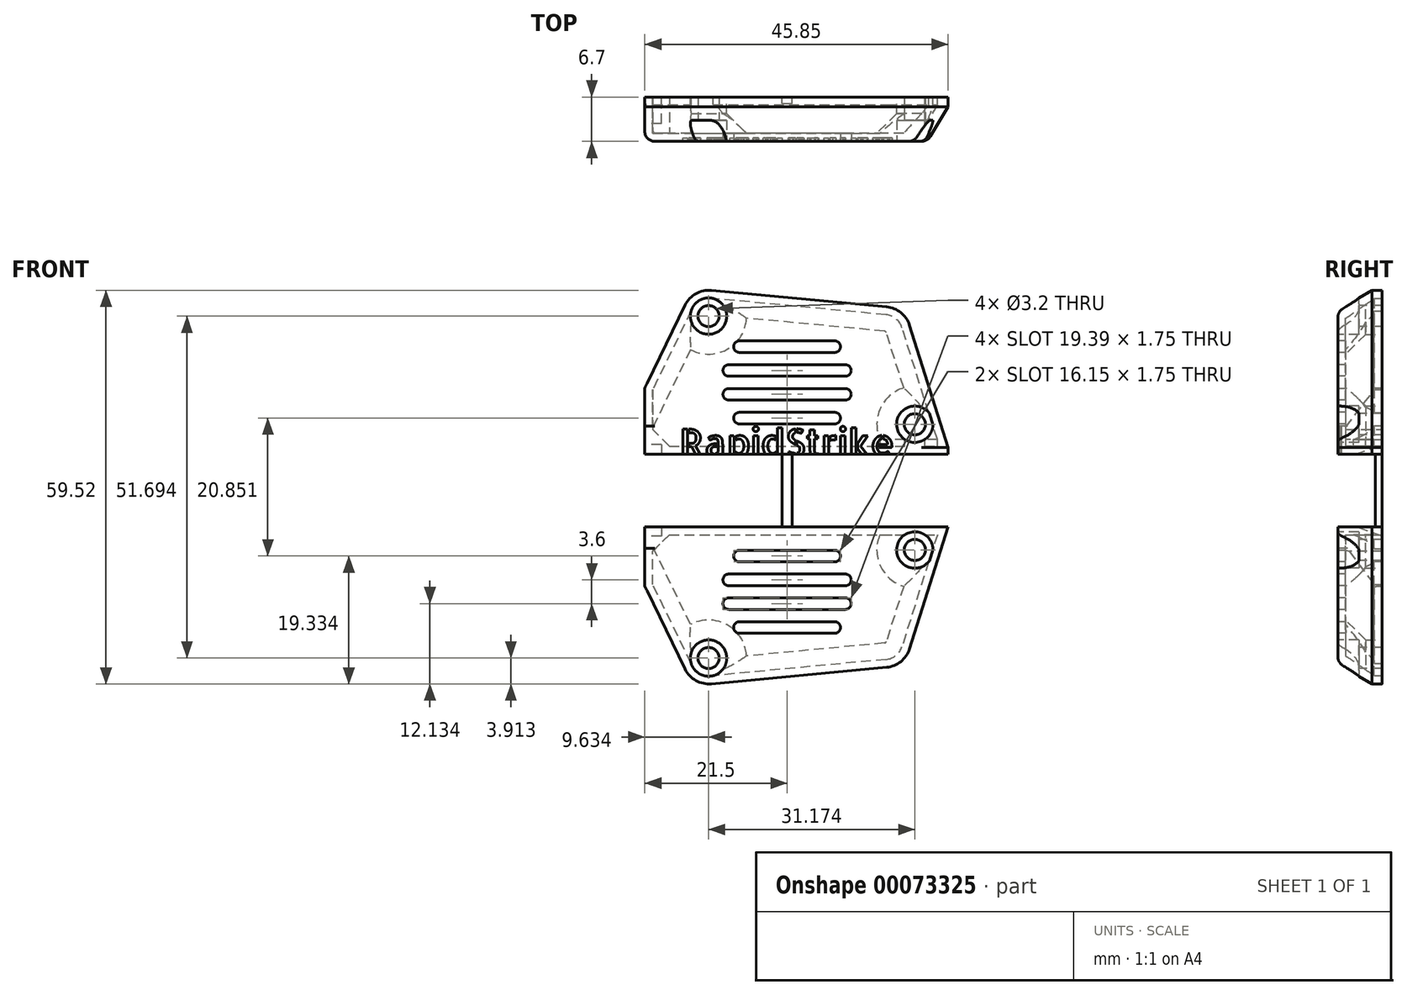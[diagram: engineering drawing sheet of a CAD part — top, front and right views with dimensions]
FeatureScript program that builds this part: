
annotation { "Feature Type Name" : "Feature", "Feature Type Description" : "" }
export const myFeature = defineFeature(function(context is Context, id is Id, definition is map)
    precondition{}
    {
        {
            var Q0;
            Q0=qCreatedBy(makeId("Front.planeOp"),FACE);
            var sketch = newSketch(context, id + "F0", { "sketchPlane" : qUnion([Q0])});
            skLineSegment(sketch, "E0", {"start": v(-21.5, 0) * mm, "end": v(21.5, 0) * mm, "construction": true});
            skLineSegment(sketch, "E1", {"start": v(24.35, -9) * mm, "end": v(17.7, 12) * mm});
            skLineSegment(sketch, "E2", {"start": v(17.7, 12) * mm, "end": v(-14.2, 15) * mm});
            skLineSegment(sketch, "E3", {"start": v(-14.2, 15) * mm, "end": v(-21.5, 0) * mm});
            skLineSegment(sketch, "E4", {"start": v(-21.5, 0) * mm, "end": v(-21.5, -9) * mm});
            skLineSegment(sketch, "E5", {"start": v(-21.5, -9) * mm, "end": v(24.35, -9) * mm});
            skSolve(sketch);
        }
        {
            var Q0;
            Q0=qCreatedBy(makeId("Front.planeOp"),FACE);
            var sketch = newSketch(context, id + "F1", { "sketchPlane" : qUnion([Q0])});
            skLineSegment(sketch, "E6.0", {"start": v(-21.5, 0) * mm, "end": v(21.5, 0) * mm});
            skLineSegment(sketch, "E6.1", {"start": v(24.35, -9) * mm, "end": v(18.5, 9.47) * mm});
            skLineSegment(sketch, "E6.2", {"start": v(15.06, 12.25) * mm, "end": v(-11.44, 14.74) * mm});
            skLineSegment(sketch, "E6.3", {"start": v(-15.41, 12.5) * mm, "end": v(-21.5, 0) * mm});
            skLineSegment(sketch, "E6.4", {"start": v(-21.5, 0) * mm, "end": v(-21.5, -9) * mm});
            skLineSegment(sketch, "E6.5", {"start": v(-21.5, -9) * mm, "end": v(24.35, -9) * mm});
            skPoint(sketch, "E7.visualSharp", {"position": v(-14.2, 15) * mm});
            skArc(sketch, "E7.filletArc", {"start": v(-11.44, 14.74) * mm, "mid": v(-13.78, 14.25) * mm, "end": v(-15.41, 12.5) * mm});
            skPoint(sketch, "E8.visualSharp", {"position": v(17.7, 12) * mm});
            skArc(sketch, "E8.filletArc", {"start": v(18.5, 9.47) * mm, "mid": v(17.2, 11.38) * mm, "end": v(15.06, 12.25) * mm});
            skSolve(sketch);
        }
        {
            var Q0;
            Q0 = qSketchRegion(id + "F1", true);
            extrude(context, id + "F2", {"entities" : qUnion([Q0]), "depth" : 6.7 * mm});
        }
        {
            var Q0;
            Q0=makeQuery(id+"F2.opExtrude","CAP_EDGE",EDGE,{"disambiguationData":[OSD([sQuery(id+"F1.wireOp",EDGE,"E6.3")])],"isStart":false});
            chamfer(context, id + "F3", {"entities" : qUnion([Q0]), "chamferType" : ChamferType.OFFSET_ANGLE, "width" : 3 * mm, "oppositeDirection" : false, "angle" : 60 * degree, "tangentPropagation" : true});
        }
        {
            var Q0;
            Q0=makeQuery(id+"F2.opExtrude","CAP_FACE",FACE,{"disambiguationData":[OSD([sQuery(id+"F1.wireOp",EDGE,"E6.1"),sQuery(id+"F1.wireOp",EDGE,"E6.2"),sQuery(id+"F1.wireOp",EDGE,"E6.3"),sQuery(id+"F1.wireOp",EDGE,"E6.4"),sQuery(id+"F1.wireOp",EDGE,"E6.5"),sQuery(id+"F1.wireOp",EDGE,"E7.filletArc"),sQuery(id+"F1.wireOp",EDGE,"E8.filletArc")])],"isStart":true});
            shell(context, id + "F4", {"entities" : qUnion([Q0]), "thickness" : 1.2 * mm});
        }
        {
            var Q0;
            Q0=makeQuery(id+"F2.opExtrude","CAP_FACE",FACE,{"disambiguationData":[OSD([sQuery(id+"F1.wireOp",EDGE,"E6.1"),sQuery(id+"F1.wireOp",EDGE,"E6.2"),sQuery(id+"F1.wireOp",EDGE,"E6.3"),sQuery(id+"F1.wireOp",EDGE,"E6.4"),sQuery(id+"F1.wireOp",EDGE,"E6.5"),sQuery(id+"F1.wireOp",EDGE,"E7.filletArc"),sQuery(id+"F1.wireOp",EDGE,"E8.filletArc")])],"isStart":false});
            var sketch = newSketch(context, id + "F5", { "sketchPlane" : qUnion([Q0])});
            skLineSegment(sketch, "E9", {"start": v(-7.2, -4.57) * mm, "end": v(7.2, -4.57) * mm});
            skLineSegment(sketch, "E10", {"start": v(8.82, -0.97) * mm, "end": v(-8.82, -0.97) * mm});
            skLineSegment(sketch, "E11", {"start": v(-8.82, 2.63) * mm, "end": v(8.82, 2.63) * mm});
            skLineSegment(sketch, "E12", {"start": v(7.2, 6.23) * mm, "end": v(-7.2, 6.23) * mm});
            skLineSegment(sketch, "E13", {"start": v(0, 6.23) * mm, "end": v(0, 2.63) * mm, "construction": true});
            skLineSegment(sketch, "E14", {"start": v(0, 2.63) * mm, "end": v(0, -0.97) * mm, "construction": true});
            skLineSegment(sketch, "E15", {"start": v(0, -0.97) * mm, "end": v(0, -4.57) * mm, "construction": true});
            skCircle(sketch, "E16", {"center": v(0, 0.83) * mm, "radius": 9 * mm});
            skLineSegment(sketch, "E17", {"start": v(0, 6.23) * mm, "end": v(0, 9.83) * mm, "construction": true});
            skLineSegment(sketch, "E18", {"start": v(0, -4.57) * mm, "end": v(0, -8.17) * mm, "construction": true});
            skLineSegment(sketch, "E19", {"start": v(0, -8.17) * mm, "end": v(0, -9) * mm, "construction": true});
            skLineSegment(sketch, "E20", {"start": v(0, 9.83) * mm, "end": v(0, 10.65) * mm, "construction": true});
            skSolve(sketch);
        }
        {
            var Q0;
            Q0=makeQuery(id+"F2.opExtrude","CAP_FACE",FACE,{"disambiguationData":[OSD([sQuery(id+"F1.wireOp",EDGE,"E6.1"),sQuery(id+"F1.wireOp",EDGE,"E6.2"),sQuery(id+"F1.wireOp",EDGE,"E6.3"),sQuery(id+"F1.wireOp",EDGE,"E6.4"),sQuery(id+"F1.wireOp",EDGE,"E6.5"),sQuery(id+"F1.wireOp",EDGE,"E7.filletArc"),sQuery(id+"F1.wireOp",EDGE,"E8.filletArc")])],"isStart":false});
            var sketch = newSketch(context, id + "F6", { "sketchPlane" : qUnion([Q0])});
            skLineSegment(sketch, "E21.JKp.JKp", {"start": v(7.2, 6.23) * mm, "end": v(-7.2, 6.23) * mm, "construction": true});
            skLineSegment(sketch, "E21.JKd.JKd", {"start": v(-8.82, 2.63) * mm, "end": v(8.82, 2.63) * mm, "construction": true});
            skLineSegment(sketch, "E21.JKF.JKF", {"start": v(-7.2, -4.57) * mm, "end": v(7.2, -4.57) * mm, "construction": true});
            skLineSegment(sketch, "E21.JKR.JKR", {"start": v(8.82, -0.97) * mm, "end": v(-8.82, -0.97) * mm, "construction": true});
            skArc(sketch, "E22.0.startCap", {"start": v(-7.2, -5.45) * mm, "mid": v(-8.07, -4.57) * mm, "end": v(-7.2, -3.7) * mm});
            skArc(sketch, "E22.0.endCap", {"start": v(7.2, -3.7) * mm, "mid": v(8.07, -4.57) * mm, "end": v(7.2, -5.45) * mm});
            skLineSegment(sketch, "E22.0.left", {"start": v(-7.2, -3.7) * mm, "end": v(7.2, -3.7) * mm});
            skLineSegment(sketch, "E22.0.right", {"start": v(-7.2, -5.45) * mm, "end": v(7.2, -5.45) * mm});
            skArc(sketch, "E22.1.startCap", {"start": v(8.82, -0.1) * mm, "mid": v(9.7, -0.97) * mm, "end": v(8.82, -1.85) * mm});
            skArc(sketch, "E22.1.endCap", {"start": v(-8.82, -1.85) * mm, "mid": v(-9.7, -0.97) * mm, "end": v(-8.82, -0.1) * mm});
            skLineSegment(sketch, "E22.1.left", {"start": v(8.82, -1.85) * mm, "end": v(-8.82, -1.85) * mm});
            skLineSegment(sketch, "E22.1.right", {"start": v(8.82, -0.1) * mm, "end": v(-8.82, -0.1) * mm});
            skArc(sketch, "E22.2.startCap", {"start": v(-8.82, 1.75) * mm, "mid": v(-9.7, 2.63) * mm, "end": v(-8.82, 3.5) * mm});
            skArc(sketch, "E22.2.endCap", {"start": v(8.82, 3.5) * mm, "mid": v(9.7, 2.63) * mm, "end": v(8.82, 1.75) * mm});
            skLineSegment(sketch, "E22.2.left", {"start": v(-8.82, 3.5) * mm, "end": v(8.82, 3.5) * mm});
            skLineSegment(sketch, "E22.2.right", {"start": v(-8.82, 1.75) * mm, "end": v(8.82, 1.75) * mm});
            skArc(sketch, "E22.3.startCap", {"start": v(7.2, 7.1) * mm, "mid": v(8.08, 6.23) * mm, "end": v(7.2, 5.35) * mm});
            skArc(sketch, "E22.3.endCap", {"start": v(-7.2, 5.35) * mm, "mid": v(-8.08, 6.23) * mm, "end": v(-7.2, 7.1) * mm});
            skLineSegment(sketch, "E22.3.left", {"start": v(7.2, 5.35) * mm, "end": v(-7.2, 5.35) * mm});
            skLineSegment(sketch, "E22.3.right", {"start": v(7.2, 7.1) * mm, "end": v(-7.2, 7.1) * mm});
            skSolve(sketch);
        }
        {
            var Q0;
            Q0 = qSketchRegion(id + "F6", true);
            extrude(context, id + "F7", {"entities" : qUnion([Q0]), "operationType" : NewBodyOperationType.REMOVE, "endBound" : BoundingType.THROUGH_ALL, "oppositeDirection" : true, "depth" : .5 * mm});
        }
        {
            var Q0;
            Q0=qCreatedBy(makeId("Top.planeOp"),FACE);
            cPlane(context, id + "F8", {"entities" : qUnion([Q0]), "cplaneType" : CPlaneType.OFFSET, "offset" : 15 * mm, "oppositeDirection" : true, "width" : 150 * mm, "height" : 150 * mm});
        }
        {
            var Q0;
            Q0=makeQuery(id+"F2.opExtrude","CAP_EDGE",EDGE,{"disambiguationData":[OSD([sQuery(id+"F1.wireOp",EDGE,"E6.4")])],"isStart":false});
            var Q1;
            {var subQ0=sQuery(id+"F1.wireOp",EDGE,"E6.3");Q1=makeQuery(id+"F3.opChamfer","BLEND_EDGE",EDGE,{"blendedFrom":[makeQuery(id+"F2.opExtrude","CAP_EDGE",EDGE,{"disambiguationData":[OSD([subQ0])],"isStart":false}),makeQuery(id+"F2.opExtrude","CAP_FACE",FACE,{"disambiguationData":[OSD([sQuery(id+"F1.wireOp",EDGE,"E6.1"),sQuery(id+"F1.wireOp",EDGE,"E6.2"),subQ0,sQuery(id+"F1.wireOp",EDGE,"E6.4"),sQuery(id+"F1.wireOp",EDGE,"E6.5"),sQuery(id+"F1.wireOp",EDGE,"E7.filletArc"),sQuery(id+"F1.wireOp",EDGE,"E8.filletArc")])],"isStart":false})],"blendedInto":[makeQuery(id+"F2.opExtrude","CAP_FACE",FACE,{"disambiguationData":[OSD([sQuery(id+"F1.wireOp",EDGE,"E6.1"),sQuery(id+"F1.wireOp",EDGE,"E6.2"),subQ0,sQuery(id+"F1.wireOp",EDGE,"E6.4"),sQuery(id+"F1.wireOp",EDGE,"E6.5"),sQuery(id+"F1.wireOp",EDGE,"E7.filletArc"),sQuery(id+"F1.wireOp",EDGE,"E8.filletArc")])],"isStart":false})]});}
            var Q2;
            Q2=makeQuery(id+"F3.opChamfer","BLEND_EDGE",EDGE,{"blendedFrom":[makeQuery(id+"F2.opExtrude","CAP_EDGE",EDGE,{"disambiguationData":[OSD([sQuery(id+"F1.wireOp",EDGE,"E6.3")])],"isStart":false}),makeQuery(id+"F2.opExtrude","SWEPT_FACE",FACE,{"disambiguationData":[OSD([sQuery(id+"F1.wireOp",EDGE,"E6.4")])]})],"blendedInto":[makeQuery(id+"F2.opExtrude","SWEPT_FACE",FACE,{"disambiguationData":[OSD([sQuery(id+"F1.wireOp",EDGE,"E6.4")])]})]});
            fillet(context, id + "F9", {"entities" : qUnion([Q0, Q1, Q2]), "radius" : 1.5 * mm, "tangentPropagation" : true, "allowEdgeOverflow" : false});
        }
        {
            var Q0;
            Q0=makeQuery(id+"F2.opExtrude","CAP_FACE",FACE,{"disambiguationData":[OSD([sQuery(id+"F1.wireOp",EDGE,"E6.1"),sQuery(id+"F1.wireOp",EDGE,"E6.2"),sQuery(id+"F1.wireOp",EDGE,"E6.3"),sQuery(id+"F1.wireOp",EDGE,"E6.4"),sQuery(id+"F1.wireOp",EDGE,"E6.5"),sQuery(id+"F1.wireOp",EDGE,"E7.filletArc"),sQuery(id+"F1.wireOp",EDGE,"E8.filletArc")])],"isStart":false});
            var sketch = newSketch(context, id + "F10", { "sketchPlane" : qUnion([Q0])});
            skCircle(sketch, "E23", {"center": v(-11.87, 10.85) * mm, "radius": 1.6 * mm});
            skCircle(sketch, "E24", {"center": v(-11.87, 10.85) * mm, "radius": 2.75 * mm});
            skCircle(sketch, "E25", {"center": v(19.3, -5.5) * mm, "radius": 1.6 * mm});
            skCircle(sketch, "E26", {"center": v(19.3, -5.5) * mm, "radius": 2.75 * mm});
            skLineSegment(sketch, "E27", {"start": v(19.3, -9) * mm, "end": v(19.3, -8.25) * mm, "construction": true});
            skLineSegment(sketch, "E28", {"start": v(-11.6, 13.59) * mm, "end": v(-11.86, 10.9) * mm, "construction": true});
            skLineSegment(sketch, "E29", {"start": v(-11.91, 10.87) * mm, "end": v(-14.34, 12.05) * mm, "construction": true});
            skLineSegment(sketch, "E30", {"start": v(21.93, -4.67) * mm, "end": v(22.88, -4.37) * mm});
            skSolve(sketch);
        }
        {
            var Q0;
            Q0=makeQuery(id+"F2.opExtrude","CAP_FACE",FACE,{"disambiguationData":[OSD([sQuery(id+"F1.wireOp",EDGE,"E6.1"),sQuery(id+"F1.wireOp",EDGE,"E6.2"),sQuery(id+"F1.wireOp",EDGE,"E6.3"),sQuery(id+"F1.wireOp",EDGE,"E6.4"),sQuery(id+"F1.wireOp",EDGE,"E6.5"),sQuery(id+"F1.wireOp",EDGE,"E7.filletArc"),sQuery(id+"F1.wireOp",EDGE,"E8.filletArc")])],"isStart":true});
            var sketch = newSketch(context, id + "F11", { "sketchPlane" : qUnion([Q0])});
            skCircle(sketch, "E31.0", {"center": v(-19.3, -5.5) * mm, "radius": 2.75 * mm});
            skCircle(sketch, "E31.1", {"center": v(11.87, 10.85) * mm, "radius": 2.75 * mm});
            skSolve(sketch);
        }
        {
            var Q0;
            Q0 = qSketchRegion(id + "F11", true);
            var Q1;
            Q1=makeQuery(id+"F2.opExtrude","SWEPT_BODY",BODY,{"disambiguationData":[OSD([sQuery(id+"F1.wireOp",EDGE,"E6.1"),sQuery(id+"F1.wireOp",EDGE,"E6.2"),sQuery(id+"F1.wireOp",EDGE,"E6.3"),sQuery(id+"F1.wireOp",EDGE,"E6.4"),sQuery(id+"F1.wireOp",EDGE,"E6.5"),sQuery(id+"F1.wireOp",EDGE,"E7.filletArc"),sQuery(id+"F1.wireOp",EDGE,"E8.filletArc")])]});
            extrude(context, id + "F12", {"entities" : qUnion([Q0]), "operationType" : NewBodyOperationType.ADD, "endBound" : BoundingType.UP_TO_BODY, "oppositeDirection" : true, "endBoundEntityBody" : qUnion([Q1]), "depth" : 25 * mm});
        }
        {
            var Q0;
            Q0=makeQuery(id+"F10.imprint","IMPRINT",FACE,{"disambiguationData":[TD([[makeQuery(id+"F10.imprint","IMPRINT",EDGE,{"derivedFrom":sQuery(id+"F10.wireOp",EDGE,"E26")}),-1.0]])]});
            var sketch = newSketch(context, id + "F13", { "sketchPlane" : qUnion([Q0])});
            skCircle(sketch, "E32.0", {"center": v(-11.87, 10.85) * mm, "radius": 1.6 * mm});
            skCircle(sketch, "E32.1", {"center": v(19.3, -5.5) * mm, "radius": 1.6 * mm});
            skSolve(sketch);
        }
        {
            var Q0;
            Q0 = qSketchRegion(id + "F13", true);
            extrude(context, id + "F14", {"entities" : qUnion([Q0]), "operationType" : NewBodyOperationType.REMOVE, "endBound" : BoundingType.THROUGH_ALL, "oppositeDirection" : true, "depth" : 25 * mm});
        }
        {
            var Q0;
            Q0=makeQuery(id+"F12.boolean.opBoolean","INTERSECT",EDGE,{"derivedFrom":[makeQuery(id+"F4.opShell","OFFSET_FACE",FACE,{"disambiguationData":[OSD([sQuery(id+"F1.wireOp",EDGE,"E6.1"),sQuery(id+"F1.wireOp",EDGE,"E6.2"),sQuery(id+"F1.wireOp",EDGE,"E6.3"),sQuery(id+"F1.wireOp",EDGE,"E6.4"),sQuery(id+"F1.wireOp",EDGE,"E6.5"),sQuery(id+"F1.wireOp",EDGE,"E7.filletArc"),sQuery(id+"F1.wireOp",EDGE,"E8.filletArc")])]}),makeQuery(id+"F12.opExtrude","SWEPT_FACE",FACE,{"disambiguationData":[OSD([sQuery(id+"F11.wireOp",EDGE,"E31.1")])]})]});
            var Q1;
            Q1=makeQuery(id+"F12.boolean.opBoolean","INTERSECT",EDGE,{"derivedFrom":[makeQuery(id+"F4.opShell","OFFSET_FACE",FACE,{"disambiguationData":[OSD([sQuery(id+"F1.wireOp",EDGE,"E6.1"),sQuery(id+"F1.wireOp",EDGE,"E6.2"),sQuery(id+"F1.wireOp",EDGE,"E6.3"),sQuery(id+"F1.wireOp",EDGE,"E6.4"),sQuery(id+"F1.wireOp",EDGE,"E6.5"),sQuery(id+"F1.wireOp",EDGE,"E7.filletArc"),sQuery(id+"F1.wireOp",EDGE,"E8.filletArc")])]}),makeQuery(id+"F12.opExtrude","SWEPT_FACE",FACE,{"disambiguationData":[OSD([sQuery(id+"F11.wireOp",EDGE,"E31.0")])]})]});
            chamfer(context, id + "F15", {"entities" : qUnion([Q0, Q1]), "width" : 3 * mm, "tangentPropagation" : true});
        }
        {
            var Q0;
            Q0=makeQuery(id+"F2.opExtrude","CAP_FACE",FACE,{"disambiguationData":[OSD([sQuery(id+"F1.wireOp",EDGE,"E6.1"),sQuery(id+"F1.wireOp",EDGE,"E6.2"),sQuery(id+"F1.wireOp",EDGE,"E6.3"),sQuery(id+"F1.wireOp",EDGE,"E6.4"),sQuery(id+"F1.wireOp",EDGE,"E6.5"),sQuery(id+"F1.wireOp",EDGE,"E7.filletArc"),sQuery(id+"F1.wireOp",EDGE,"E8.filletArc")])],"isStart":false});
            var sketch = newSketch(context, id + "F16", { "sketchPlane" : qUnion([Q0])});
            skCircle(sketch, "E33.0", {"center": v(-11.87, 10.85) * mm, "radius": 2.75 * mm});
            skCircle(sketch, "E33.1", {"center": v(19.3, -5.5) * mm, "radius": 2.75 * mm});
            skSolve(sketch);
        }
        {
            var Q0;
            Q0 = qSketchRegion(id + "F16", true);
            extrude(context, id + "F17", {"entities" : qUnion([Q0]), "operationType" : NewBodyOperationType.REMOVE, "oppositeDirection" : true, "depth" : 3.2 * mm});
        }
        {
            var Q0;
            Q0=makeQuery(id+"F2.opExtrude","SWEPT_BODY",BODY,{"disambiguationData":[OSD([sQuery(id+"F1.wireOp",EDGE,"E6.1"),sQuery(id+"F1.wireOp",EDGE,"E6.2"),sQuery(id+"F1.wireOp",EDGE,"E6.3"),sQuery(id+"F1.wireOp",EDGE,"E6.4"),sQuery(id+"F1.wireOp",EDGE,"E6.5"),sQuery(id+"F1.wireOp",EDGE,"E7.filletArc"),sQuery(id+"F1.wireOp",EDGE,"E8.filletArc")])]});
            var Q1;
            Q1=qCreatedBy(id+"F8.planeOp",FACE);
            mirror(context, id + "F18", {"operationType" : NewBodyOperationType.ADD, "entities" : qUnion([Q0]), "mirrorPlane" : qUnion([Q1])});
        }
        {
            assignVariable(context, id + "F19", {"name" : "top_enlarge", "anyValue" : 1});
        }
        {
            var Q0;
            Q0=makeQuery(id+"F2.opExtrude","SWEPT_FACE",FACE,{"disambiguationData":[OSD([sQuery(id+"F1.wireOp",EDGE,"E6.5")])]});
            extrude(context, id + "F20", {"entities" : qUnion([Q0]), "operationType" : NewBodyOperationType.ADD, "depth" : (getVariable(context, 'top_enlarge')) * mm});
        }
        {
            var Q0;
            Q0=makeQuery(id+"F4.opShell","OFFSET_FACE",FACE,{"disambiguationData":[OSD([sQuery(id+"F1.wireOp",EDGE,"E6.5")])]});
            extrude(context, id + "F21", {"entities" : qUnion([Q0]), "operationType" : NewBodyOperationType.REMOVE, "oppositeDirection" : true, "depth" : (getVariable(context, 'top_enlarge')) * mm});
        }
        {
            var Q0;
            Q0=qCreatedBy(makeId("Front.planeOp"),FACE);
            var sketch = newSketch(context, id + "F22", { "sketchPlane" : qUnion([Q0])});
            skLineSegment(sketch, "E34.bottom", {"start": v(-0.75, -10) * mm, "end": v(0.75, -10) * mm});
            skLineSegment(sketch, "E34.top", {"start": v(-0.75, -21) * mm, "end": v(0.75, -21) * mm});
            skLineSegment(sketch, "E34.left", {"start": v(-0.75, -10) * mm, "end": v(-0.75, -21) * mm});
            skLineSegment(sketch, "E34.right", {"start": v(0.75, -10) * mm, "end": v(0.75, -21) * mm});
            skLineSegment(sketch, "E35", {"start": v(0, 0) * mm, "end": v(0, -10) * mm});
            skSolve(sketch);
        }
        {
            var Q0;
            Q0 = qSketchRegion(id + "F22", true);
            extrude(context, id + "F23", {"entities" : qUnion([Q0]), "operationType" : NewBodyOperationType.ADD, "depth" : 1 * mm});
        }
        {
            var Q0;
            {var subQ0=sQuery(id+"F1.wireOp",EDGE,"E6.5");Q0=makeQuery(id+"F20.boolean.opBoolean","MERGE",FACE,{"derivedFrom":[makeQuery(id+"F2.opExtrude","CAP_FACE",FACE,{"disambiguationData":[OSD([sQuery(id+"F1.wireOp",EDGE,"E6.1"),sQuery(id+"F1.wireOp",EDGE,"E6.2"),sQuery(id+"F1.wireOp",EDGE,"E6.3"),sQuery(id+"F1.wireOp",EDGE,"E6.4"),subQ0,sQuery(id+"F1.wireOp",EDGE,"E7.filletArc"),sQuery(id+"F1.wireOp",EDGE,"E8.filletArc")])],"isStart":false}),makeQuery(id+"F20.opExtrude","SWEPT_FACE",FACE,{"disambiguationData":[OSD([subQ0]),TDD([makeQuery(id+"F2.opExtrude","CAP_EDGE",EDGE,{"disambiguationData":[OSD([subQ0])],"isStart":false})])]})]});}
            var sketch = newSketch(context, id + "F24", { "sketchPlane" : qUnion([Q0])});
            skText(sketch, "E36", { "text": "RapidStrike", "fontName": "AllertaStencil-Regular.ttf"});
            skLineSegment(sketch, "E37", {"start": v(0, -9.2) * mm, "end": v(0, -10) * mm});
            skLineSegment(sketch, "E38", {"start": v(0, -6.25) * mm, "end": v(0, -5.45) * mm});
            const initialGuessF24  = {"E36": [-0.01624, -0.0104, 1, 0, 0.00415]};
            skSetInitialGuess(sketch, initialGuessF24);
            skSolve(sketch);
        }
        {
            var Q0;
            Q0 = qSketchRegion(id + "F24", true);
            extrude(context, id + "F25", {"entities" : qUnion([Q0]), "operationType" : NewBodyOperationType.REMOVE, "oppositeDirection" : true, "depth" : .5 * mm});
        }
        {
            var Q0;
            {var subQ0=sQuery(id+"F1.wireOp",EDGE,"E6.5");var subQ1=sQuery(id+"F1.wireOp",EDGE,"E6.4");Q0=makeQuery(id+"F20.boolean.opBoolean","MERGE",FACE,{"derivedFrom":[makeQuery(id+"F2.opExtrude","SWEPT_FACE",FACE,{"disambiguationData":[OSD([subQ1])]}),makeQuery(id+"F20.opExtrude","SWEPT_FACE",FACE,{"disambiguationData":[OSD([subQ1,subQ0]),TDD([makeQuery(id+"F2.opExtrude","SWEPT_EDGE",EDGE,{"disambiguationData":[OSD([subQ1,subQ0])]})])]})]});}
            var sketch = newSketch(context, id + "F26", { "sketchPlane" : qUnion([Q0])});
            skLineSegment(sketch, "E39", {"start": v(4, -10) * mm, "end": v(0, -8.6) * mm});
            skLineSegment(sketch, "E40", {"start": v(0, -8.6) * mm, "end": v(0, -10) * mm});
            skLineSegment(sketch, "E41", {"start": v(0, -10) * mm, "end": v(4, -10) * mm});
            skLineSegment(sketch, "E42", {"start": v(4, -21) * mm, "end": v(0, -21) * mm});
            skLineSegment(sketch, "E43", {"start": v(0, -21) * mm, "end": v(0, -22.4) * mm});
            skLineSegment(sketch, "E44", {"start": v(0, -22.4) * mm, "end": v(4, -21) * mm});
            skSolve(sketch);
        }
        {
            var Q0;
            Q0 = qSketchRegion(id + "F26", true);
            extrude(context, id + "F27", {"entities" : qUnion([Q0]), "operationType" : NewBodyOperationType.REMOVE, "oppositeDirection" : true, "depth" : 2.5 * mm});
        }
        {
            var Q0;
            Q0=makeQuery(id+"F21.boolean.opBoolean","COPY",EDGE,{"derivedFrom":makeQuery(id+"F21.opExtrude","CAP_EDGE",EDGE,{"disambiguationData":[OSD([sQuery(id+"F1.wireOp",EDGE,"E6.4"),sQuery(id+"F1.wireOp",EDGE,"E6.5")])],"isStart":false})});
            var Q1;
            Q1=makeQuery(id+"F18.opPattern","COPY",EDGE,{"derivedFrom":makeQuery(id+"F4.opShell","OFFSET_EDGE",EDGE,{"disambiguationData":[OSD([sQuery(id+"F1.wireOp",EDGE,"E6.4"),sQuery(id+"F1.wireOp",EDGE,"E6.5")])]}),"instanceName":"1"});
            chamfer(context, id + "F28", {"entities" : qUnion([Q0, Q1]), "width" : 2.5 * mm, "tangentPropagation" : true});
        }
    });
